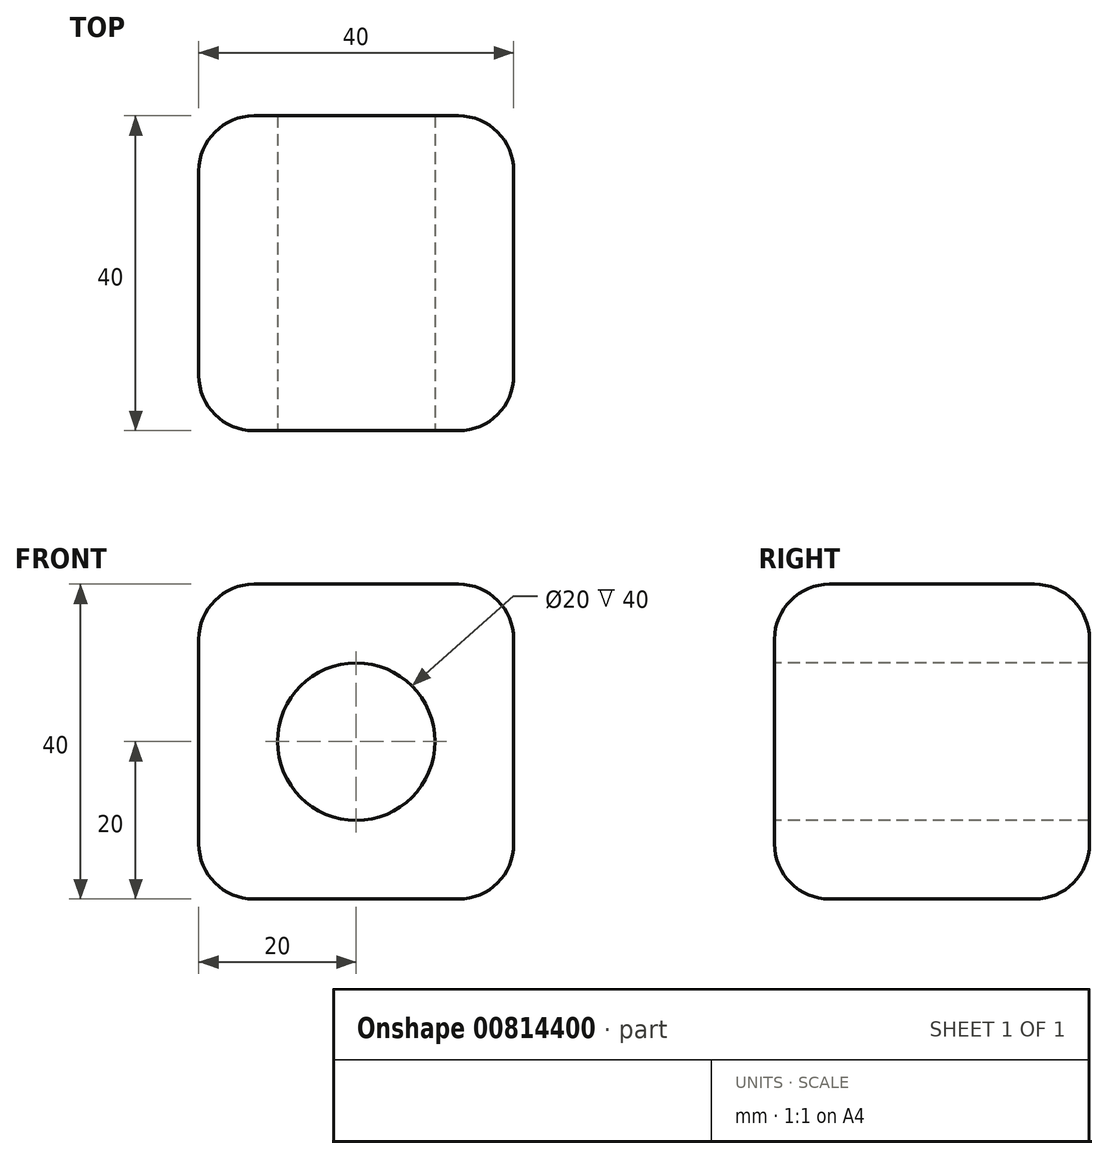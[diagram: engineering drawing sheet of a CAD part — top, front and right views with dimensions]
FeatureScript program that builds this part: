
annotation { "Feature Type Name" : "Feature", "Feature Type Description" : "" }
export const myFeature = defineFeature(function(context is Context, id is Id, definition is map)
    precondition{}
    {
        {
            var Q0;
            Q0=qCreatedBy(makeId("Front.planeOp"),FACE);
            var sketch = newSketch(context, id + "F0", { "sketchPlane" : qUnion([Q0])});
            skLineSegment(sketch, "E0.bottom", {"start": v(0, 0) * mm, "end": v(40, 0) * mm});
            skLineSegment(sketch, "E0.top", {"start": v(0, 40) * mm, "end": v(40, 40) * mm});
            skLineSegment(sketch, "E0.left", {"start": v(0, 0) * mm, "end": v(0, 40) * mm});
            skLineSegment(sketch, "E0.right", {"start": v(40, 0) * mm, "end": v(40, 40) * mm});
            skSolve(sketch);
        }
        {
            var Q0;
            Q0=makeQuery(id+"F0.imprint","IMPRINT",FACE,{"disambiguationData":[TD([[makeQuery(id+"F0.imprint","IMPRINT",EDGE,{"derivedFrom":sQuery(id+"F0.wireOp",EDGE,"E0.bottom")}),1.0]])]});
            extrude(context, id + "F1", {"entities" : qUnion([Q0]), "depth" : 40 * mm, "offsetDistance" : 25 * mm});
        }
        {
            var Q0;
            Q0=makeQuery(id+"F1.opExtrude","SWEPT_FACE",FACE,{"disambiguationData":[OSD([sQuery(id+"F0.wireOp",EDGE,"E0.top")])]});
            var Q1;
            Q1=makeQuery(id+"F1.opExtrude","CAP_FACE",FACE,{"disambiguationData":[OSD([sQuery(id+"F0.wireOp",EDGE,"E0.bottom"),sQuery(id+"F0.wireOp",EDGE,"E0.top"),sQuery(id+"F0.wireOp",EDGE,"E0.left"),sQuery(id+"F0.wireOp",EDGE,"E0.right")])],"isStart":false});
            var Q2;
            Q2=makeQuery(id+"F1.opExtrude","SWEPT_FACE",FACE,{"disambiguationData":[OSD([sQuery(id+"F0.wireOp",EDGE,"E0.left")])]});
            var Q3;
            Q3=makeQuery(id+"F1.opExtrude","CAP_FACE",FACE,{"disambiguationData":[OSD([sQuery(id+"F0.wireOp",EDGE,"E0.bottom"),sQuery(id+"F0.wireOp",EDGE,"E0.top"),sQuery(id+"F0.wireOp",EDGE,"E0.left"),sQuery(id+"F0.wireOp",EDGE,"E0.right")])],"isStart":true});
            var Q4;
            Q4=makeQuery(id+"F1.opExtrude","SWEPT_FACE",FACE,{"disambiguationData":[OSD([sQuery(id+"F0.wireOp",EDGE,"E0.right")])]});
            fillet(context, id + "F2", {"entities" : qUnion([Q0, Q1, Q2, Q3, Q4]), "radius" : 7 * mm, "tangentPropagation" : true, "allowEdgeOverflow" : false});
        }
        {
            var Q0;
            Q0=makeQuery(id+"F1.opExtrude","CAP_FACE",FACE,{"disambiguationData":[OSD([sQuery(id+"F0.wireOp",EDGE,"E0.bottom"),sQuery(id+"F0.wireOp",EDGE,"E0.top"),sQuery(id+"F0.wireOp",EDGE,"E0.left"),sQuery(id+"F0.wireOp",EDGE,"E0.right")])],"isStart":false});
            var sketch = newSketch(context, id + "F3", { "sketchPlane" : qUnion([Q0])});
            skCircle(sketch, "E1", {"center": v(20, 20) * mm, "radius": 10 * mm});
            skSolve(sketch);
        }
        {
            var Q0;
            Q0=makeQuery(id+"F3.imprint","IMPRINT",FACE,{"disambiguationData":[TD([[makeQuery(id+"F3.imprint","IMPRINT",EDGE,{"derivedFrom":sQuery(id+"F3.wireOp",EDGE,"E1")}),1.0]])]});
            extrude(context, id + "F4", {"entities" : qUnion([Q0]), "operationType" : NewBodyOperationType.REMOVE, "oppositeDirection" : true, "depth" : 50 * mm, "offsetDistance" : 25 * mm});
        }
    });
